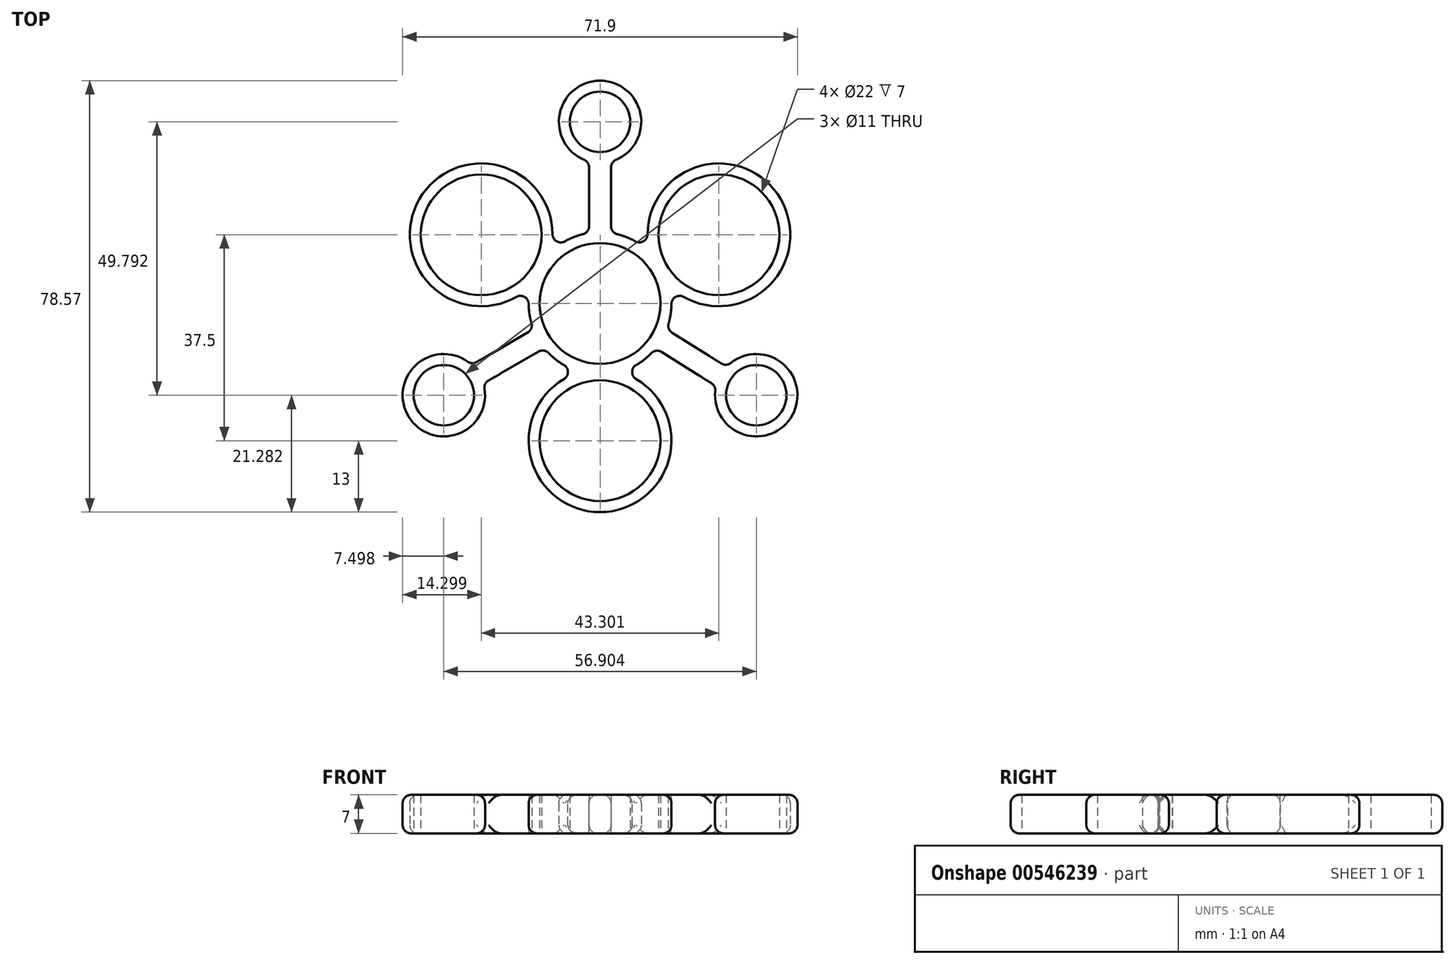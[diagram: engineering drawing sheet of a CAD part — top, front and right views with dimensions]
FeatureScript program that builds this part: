
annotation { "Feature Type Name" : "Feature", "Feature Type Description" : "" }
export const myFeature = defineFeature(function(context is Context, id is Id, definition is map)
    precondition{}
    {
        {
            var Q0;
            Q0=qCreatedBy(makeId("Top.planeOp"),FACE);
            var sketch = newSketch(context, id + "F0", { "sketchPlane" : qUnion([Q0])});
            skCircle(sketch, "E0", {"center": v(0, 0) * mm, "radius": 11 * mm});
            skCircle(sketch, "E1", {"center": v(0, 33.07) * mm, "radius": 5.5 * mm});
            skCircle(sketch, "E2", {"center": v(-28.45, -16.72) * mm, "radius": 5.5 * mm});
            skCircle(sketch, "E3", {"center": v(28.45, -16.72) * mm, "radius": 5.5 * mm});
            skCircle(sketch, "E4", {"center": v(0, 33.07) * mm, "radius": 7.5 * mm});
            skCircle(sketch, "E5", {"center": v(-28.45, -16.72) * mm, "radius": 7.5 * mm});
            skCircle(sketch, "E6", {"center": v(28.45, -16.72) * mm, "radius": 7.5 * mm});
            skCircle(sketch, "E7", {"center": v(0, 0) * mm, "radius": 13 * mm});
            skLineSegment(sketch, "E8", {"start": v(-12.12, -4.7) * mm, "end": v(-23.38, -11.2) * mm});
            skLineSegment(sketch, "E9", {"start": v(-10.12, -8.15) * mm, "end": v(-21.26, -14.58) * mm});
            skLineSegment(sketch, "E10", {"start": v(12.13, -4.69) * mm, "end": v(23.03, -11.53) * mm});
            skLineSegment(sketch, "E11", {"start": v(21.14, -15.06) * mm, "end": v(10.12, -8.15) * mm});
            skLineSegment(sketch, "E12", {"start": v(-2, 25.85) * mm, "end": v(-2, 12.85) * mm});
            skLineSegment(sketch, "E13", {"start": v(2, 25.85) * mm, "end": v(2, 12.85) * mm});
            skLineSegment(sketch, "E14", {"start": v(0, 0) * mm, "end": v(0, -69.77) * mm, "construction": true});
            skLineSegment(sketch, "E15", {"start": v(0, 0) * mm, "end": v(-61.9, 35.74) * mm, "construction": true});
            skLineSegment(sketch, "E16", {"start": v(0, 0) * mm, "end": v(58.14, 33.57) * mm, "construction": true});
            skCircle(sketch, "E17", {"center": v(-21.65, 12.5) * mm, "radius": 11 * mm});
            skCircle(sketch, "E18", {"center": v(-21.65, 12.5) * mm, "radius": 13 * mm});
            skCircle(sketch, "E19", {"center": v(0, -25) * mm, "radius": 11 * mm});
            skCircle(sketch, "E20", {"center": v(0, -25) * mm, "radius": 13 * mm});
            skCircle(sketch, "E21", {"center": v(21.65, 12.5) * mm, "radius": 11 * mm});
            skCircle(sketch, "E22", {"center": v(21.65, 12.5) * mm, "radius": 13 * mm});
            skSolve(sketch);
        }
        {
            var Q0;
            Q0=qSketchRegion(id+"F0",true);
            var Q1;
            Q1=makeQuery(id+"F0.imprint","IMPRINT",FACE,{"disambiguationData":[TD([[makeQuery(id+"F0.imprint","IMPRINT",EDGE,{"derivedFrom":sQuery(id+"F0.wireOp",EDGE,"E0")}),-1.0]])]});
            var Q2;
            {var subQ0=sQuery(id+"F0.wireOp",EDGE,"E12");var subQ1=sQuery(id+"F0.wireOp",EDGE,"E7");var subQ2=makeQuery(id+"F0.imprint","INTERSECT",VERTEX,{"derivedFrom":[subQ1,subQ0]});Q2=makeQuery(id+"F0.imprint","IMPRINT",FACE,{"disambiguationData":[TD([[makeQuery(id+"F0.imprint","IMPRINT",EDGE,{"disambiguationData":[TD([[subQ2,1.0]])],"derivedFrom":subQ1}),-1.0]])]});}
            var Q3;
            {var subQ0=sQuery(id+"F0.wireOp",EDGE,"E8");var subQ1=sQuery(id+"F0.wireOp",EDGE,"E7");var subQ2=makeQuery(id+"F0.imprint","INTERSECT",VERTEX,{"derivedFrom":[subQ1,subQ0]});Q3=makeQuery(id+"F0.imprint","IMPRINT",FACE,{"disambiguationData":[TD([[makeQuery(id+"F0.imprint","IMPRINT",EDGE,{"disambiguationData":[TD([[subQ2,-1.0]])],"derivedFrom":subQ1}),-1.0]])]});}
            var Q4;
            {var subQ0=sQuery(id+"F0.wireOp",EDGE,"E10");var subQ1=sQuery(id+"F0.wireOp",EDGE,"E7");var subQ2=makeQuery(id+"F0.imprint","INTERSECT",VERTEX,{"derivedFrom":[subQ1,subQ0]});Q4=makeQuery(id+"F0.imprint","IMPRINT",FACE,{"disambiguationData":[TD([[makeQuery(id+"F0.imprint","IMPRINT",EDGE,{"disambiguationData":[TD([[subQ2,1.0]])],"derivedFrom":subQ1}),-1.0]])]});}
            extrude(context, id + "F1", {"entities" : qUnion([Q0, Q1, Q2, Q3, Q4]), "depth" : 7 * mm, "offsetDistance" : 25 * mm});
        }
        {
            var Q0;
            Q0=makeQuery(id+"F1.opExtrude","SWEPT_FACE",FACE,{"disambiguationData":[OSD([sQuery(id+"F0.wireOp",EDGE,"E4")])]});
            var Q1;
            Q1=makeQuery(id+"F1.opExtrude","SWEPT_FACE",FACE,{"disambiguationData":[OSD([sQuery(id+"F0.wireOp",EDGE,"E22")])]});
            var Q2;
            Q2=makeQuery(id+"F1.opExtrude","SWEPT_FACE",FACE,{"disambiguationData":[OSD([sQuery(id+"F0.wireOp",EDGE,"E6")])]});
            var Q3;
            Q3=makeQuery(id+"F1.opExtrude","SWEPT_FACE",FACE,{"disambiguationData":[OSD([sQuery(id+"F0.wireOp",EDGE,"E20")])]});
            var Q4;
            Q4=makeQuery(id+"F1.opExtrude","SWEPT_FACE",FACE,{"disambiguationData":[OSD([sQuery(id+"F0.wireOp",EDGE,"E18")])]});
            var Q5;
            Q5=makeQuery(id+"F1.opExtrude","SWEPT_FACE",FACE,{"disambiguationData":[OSD([sQuery(id+"F0.wireOp",EDGE,"E5")])]});
            var Q6;
            Q6=makeQuery(id+"F1.opExtrude","SWEPT_EDGE",EDGE,{"disambiguationData":[OSD([sQuery(id+"F0.wireOp",EDGE,"E7"),sQuery(id+"F0.wireOp",EDGE,"E12")])]});
            var Q7;
            Q7=makeQuery(id+"F1.opExtrude","SWEPT_EDGE",EDGE,{"disambiguationData":[OSD([sQuery(id+"F0.wireOp",EDGE,"E7"),sQuery(id+"F0.wireOp",EDGE,"E13")])]});
            var Q8;
            Q8=makeQuery(id+"F1.opExtrude","SWEPT_EDGE",EDGE,{"disambiguationData":[OSD([sQuery(id+"F0.wireOp",EDGE,"E7"),sQuery(id+"F0.wireOp",EDGE,"E8")])]});
            var Q9;
            Q9=makeQuery(id+"F1.opExtrude","SWEPT_EDGE",EDGE,{"disambiguationData":[OSD([sQuery(id+"F0.wireOp",EDGE,"E7"),sQuery(id+"F0.wireOp",EDGE,"E9")])]});
            var Q10;
            Q10=makeQuery(id+"F1.opExtrude","SWEPT_EDGE",EDGE,{"disambiguationData":[OSD([sQuery(id+"F0.wireOp",EDGE,"E7"),sQuery(id+"F0.wireOp",EDGE,"E11")])]});
            var Q11;
            Q11=makeQuery(id+"F1.opExtrude","SWEPT_EDGE",EDGE,{"disambiguationData":[OSD([sQuery(id+"F0.wireOp",EDGE,"E7"),sQuery(id+"F0.wireOp",EDGE,"E10")])]});
            fillet(context, id + "F2", {"entities" : qUnion([Q0, Q1, Q2, Q3, Q4, Q5, Q6, Q7, Q8, Q9, Q10, Q11]), "radius" : 1.5 * mm, "tangentPropagation" : true, "allowEdgeOverflow" : false});
        }
    });
